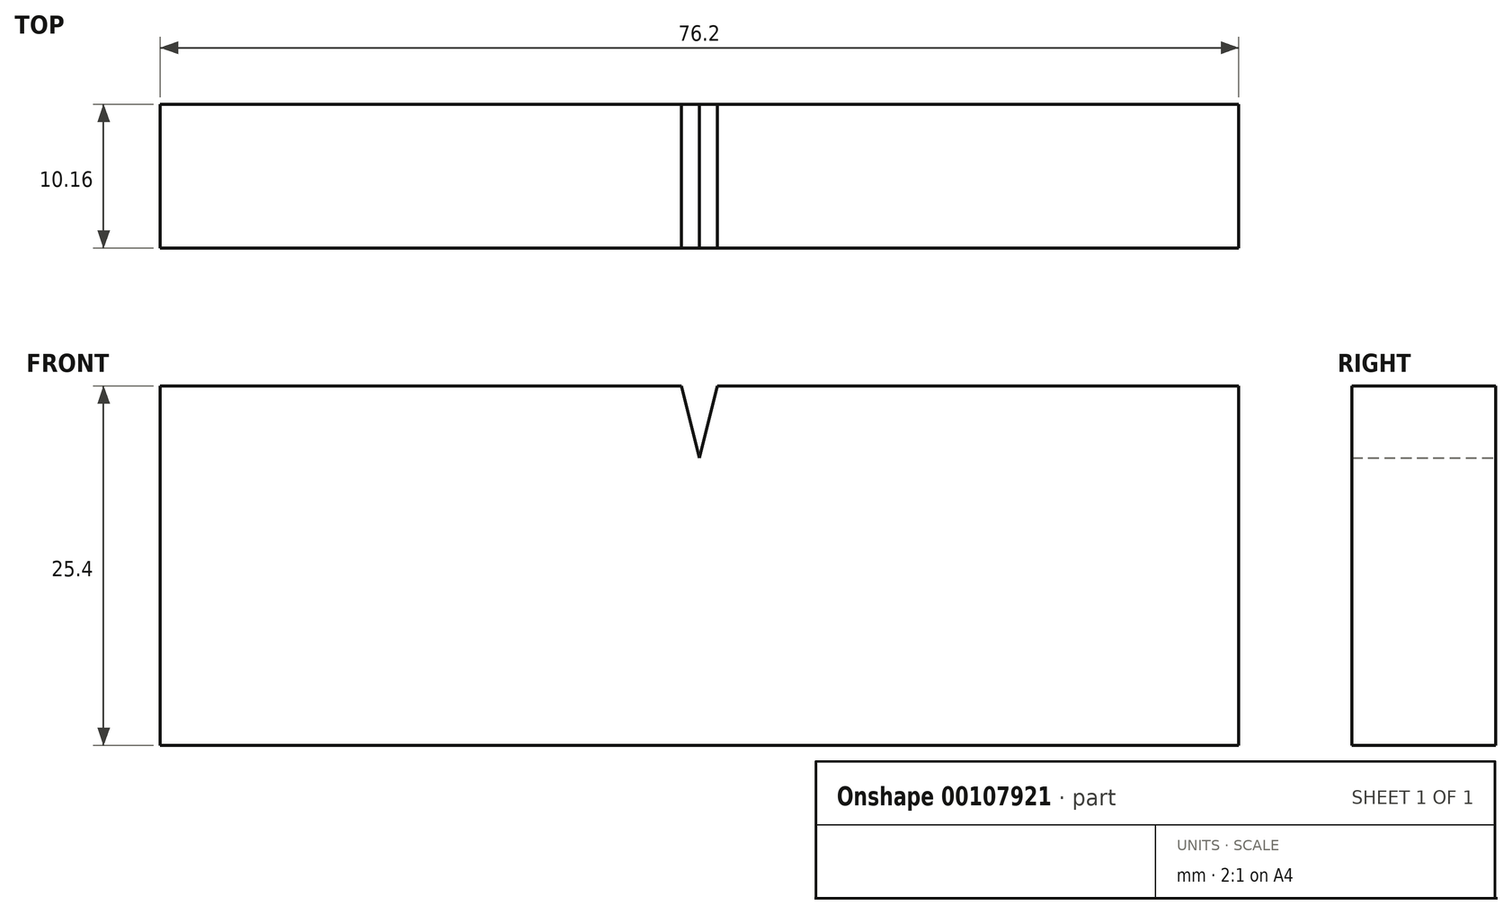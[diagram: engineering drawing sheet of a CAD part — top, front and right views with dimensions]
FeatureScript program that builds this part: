
annotation { "Feature Type Name" : "Feature", "Feature Type Description" : "" }
export const myFeature = defineFeature(function(context is Context, id is Id, definition is map)
    precondition{}
    {
        {
            var Q0;
            Q0=qCreatedBy(makeId("Front.planeOp"),FACE);
            var sketch = newSketch(context, id + "F1", { "sketchPlane" : qUnion([Q0])});
            skLineSegment(sketch, "E0.bottom", {"start": v(-36.83, 15.93) * mm, "end": v(0, 15.93) * mm});
            skLineSegment(sketch, "E0.top", {"start": v(-36.83, -9.47) * mm, "end": v(39.37, -9.47) * mm});
            skLineSegment(sketch, "E0.left", {"start": v(-36.83, 15.93) * mm, "end": v(-36.83, -9.47) * mm});
            skLineSegment(sketch, "E0.right", {"start": v(39.37, 15.93) * mm, "end": v(39.37, -9.47) * mm});
            skLineSegment(sketch, "E1", {"start": v(1.27, 10.85) * mm, "end": v(1.27, -9.47) * mm});
            skLineSegment(sketch, "E2", {"start": v(1.27, -9.47) * mm, "end": v(1.27, 10.85) * mm});
            skLineSegment(sketch, "E3", {"start": v(1.27, 10.85) * mm, "end": v(0, 15.93) * mm});
            skLineSegment(sketch, "E4", {"start": v(2.54, 15.93) * mm, "end": v(1.27, 10.85) * mm});
            skPoint(sketch, "E5.orphan", {"position": v(1.27, 15.93) * mm});
            skLineSegment(sketch, "E6.trimOffspring", {"start": v(2.54, 15.93) * mm, "end": v(39.37, 15.93) * mm});
            skSolve(sketch);
        }
        {
            var Q0;
            Q0 = qSketchRegion(id + "F1", true);
            extrude(context, id + "F0", {"entities" : qUnion([Q0]), "depth" : 10.16 * mm});
        }
    });
